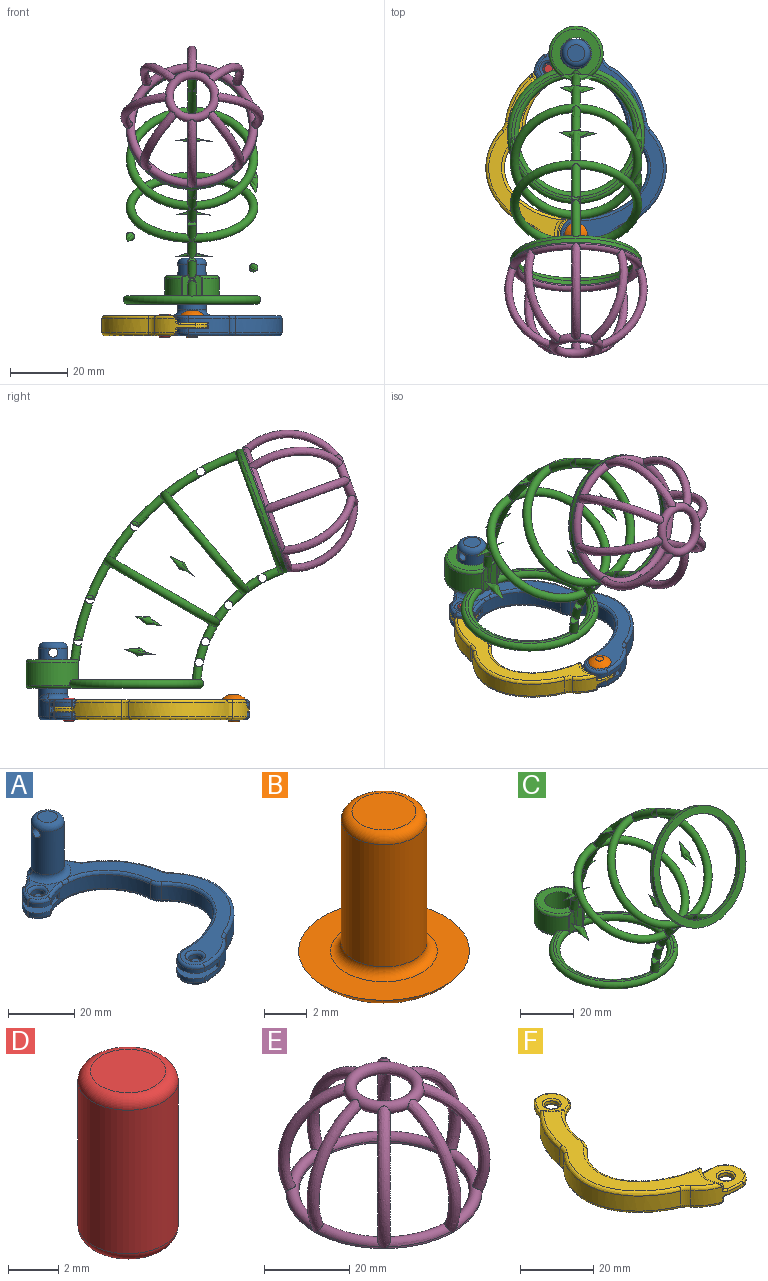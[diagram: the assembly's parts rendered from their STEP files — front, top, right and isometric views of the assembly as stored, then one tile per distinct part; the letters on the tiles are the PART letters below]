
ASSEMBLY  parts=6 mates=4
PART A: 90 faces, bbox 46.6x74.3x27 mm
  f0: plane 12.46x10.26mm, normal (0,0,1), area 30.7mm2, adj f19,f52,f55,f58,f59,f61,f85
  f1: plane 12.06x11.22mm, normal (0,0,-1), area 96.4mm2, adj f4,f12,f13,f14,f23,f88,f89
  f2: plane 12x11.67mm, normal (0,0,-1), area 80.9mm2, adj f8,f9,f10,f11,f15,f24,f38,f53
  f3: cylinder r=5mm len=18mm, axis (0,0,-1), area 498.6mm2, adj f18,f19,f20,f21,f22
  f4: extruded ~14.59x5.79mm, area 66.9mm2, adj f1,f14,f25,f27,f34,f46,f66,f89
  f5: extruded ~34.58x16.19mm, area 215.6mm2, adj f34,f35,f44,f71
  f6: extruded ~19.31x12.86mm, area 120.1mm2, adj f35,f36,f42,f76
  f7: extruded ~17.27x7.1mm, area 119.7mm2, adj f18,f20,f36,f38,f39,f40,f60,f80
  f8: cylinder r=5.28mm len=1.5mm, axis (0,0,-1), area 1.4mm2, adj f2,f9,f38,f59
  f9: extruded ~5.77x3.34mm, area 10.2mm2, adj f2,f8,f56,f58
  f10: cylinder r=5.28mm len=5.1mm, axis (0,0,-1), area 10.5mm2, adj f2,f53,f55,f56
  f11: extruded ~26.97x18.03mm, area 174.5mm2, adj f2,f26,f37,f50,f51,f52,f53,f67
  f12: extruded ~28.38x24.99mm, area 221.8mm2, adj f1,f14,f25,f27,f37,f48,f63,f88
  f13: cylinder r=2.1mm len=4.2mm, axis (0,0,-1), area 19.8mm2, adj f1,f84
  f14: cylinder r=5.53mm len=10.89mm, axis (0,0,-1), area 24mm2, adj f1,f4,f12,f47
  f15: cylinder r=2.1mm len=4.2mm, axis (0,0,-1), area 19.8mm2, adj f2,f85
  f16: plane 68.02x35.04mm, normal (0,0,1), area 436.8mm2, adj f19,f40,f41,f42,f43,f44,f45,f46
  f17: plane 6x6mm, normal (0,0,1), area 28.3mm2, adj f21
  f18: bspline ~6.9x3.63mm, area 7.6mm2, adj f3,f7,f19,f39
  f19: torus R=7mm, axis (0,0,1), area 67.5mm2, adj f0,f3,f16,f18,f20,f39,f51,f60
  f20: bspline ~6.9x3.63mm, area 7.6mm2, adj f3,f7,f19,f60
  f21: torus R=3mm, axis (0,0,1), area 84.4mm2, adj f3,f17
  f22: cylinder r=1.6mm len=10mm, axis (-1,0,0), area 100.5mm2, adj f3
  f23: cylinder r=6.53mm len=8.7mm, axis (0,0,1), area 19.2mm2, adj f1,f25,f88,f89
  f24: cylinder r=6.28mm len=7.95mm, axis (0,0,1), area 19.5mm2, adj f2,f26,f86,f87
  f25: plane 12.06x11.22mm, normal (0,0,1), area 96.4mm2, adj f4,f12,f23,f27,f32,f88,f89
  f26: plane 12x11.67mm, normal (0,0,1), area 80.9mm2, adj f11,f24,f28,f29,f30,f31,f38,f67
  f27: cylinder r=5.53mm len=10.89mm, axis (0,0,1), area 24mm2, adj f4,f12,f25,f64
  f28: cylinder r=5.28mm len=1.5mm, axis (0,0,1), area 1.4mm2, adj f26,f29,f38,f79
  f29: extruded ~5.77x3.34mm, area 10.2mm2, adj f26,f28,f72,f77
  f30: cylinder r=2.1mm len=4.2mm, axis (0,0,1), area 19.8mm2, adj f26,f83
  f31: cylinder r=5.28mm len=5.1mm, axis (0,0,1), area 10.5mm2, adj f26,f67,f72,f73
  f32: cylinder r=2.1mm len=4.2mm, axis (0,0,1), area 19.8mm2, adj f25,f82
  f33: plane 71.5x44.25mm, normal (0,0,-1), area 585.1mm2, adj f63,f64,f65,f66,f68,f69,f71,f73
  f34: cylinder r=5mm len=5mm, axis (0,0,-1), area 13.5mm2, adj f4,f5,f45,f69
  f35: cylinder r=5mm len=5mm, axis (0,0,-1), area 14.8mm2, adj f5,f6,f43,f74
  f36: cylinder r=5mm len=5mm, axis (0,0,-1), area 16.3mm2, adj f6,f7,f41,f78
  f37: cylinder r=5mm len=5mm, axis (0,0,-1), area 19mm2, adj f11,f12,f49,f65
  f38: cylinder r=5mm len=5mm, axis (0,0,-1), area 10.5mm2, adj f2,f7,f8,f26,f28,f61,f62,f81
  f39: bspline ~5.42x5.06mm, area 4.4mm2, adj f7,f18,f19,f40
  f40: bspline ~5.76x3.77mm, area 5.9mm2, adj f7,f16,f39,f41
  f41: torus R=6mm, axis (0,0,1), area 5.5mm2, adj f16,f36,f40,f42
  f42: bspline ~21.43x15.78mm, area 37.2mm2, adj f6,f16,f41,f43
  f43: torus R=6mm, axis (0,0,1), area 5mm2, adj f16,f35,f42,f44
  f44: bspline ~37.16x17.56mm, area 66.6mm2, adj f5,f16,f43,f45
  f45: torus R=6mm, axis (0,0,1), area 4.6mm2, adj f16,f34,f44,f46
  f46: bspline ~16.58x6.76mm, area 25mm2, adj f4,f16,f45,f47
  f47: torus R=4.53mm, axis (0,0,1), area 23.4mm2, adj f14,f16,f46,f48
  f48: bspline ~30.58x29.82mm, area 73.9mm2, adj f12,f16,f47,f49
  f49: torus R=4mm, axis (0,0,1), area 5.5mm2, adj f16,f37,f48,f50
  f50: bspline ~21.54x18.95mm, area 42.7mm2, adj f11,f16,f49,f51
  f51: bspline ~4.13x1.09mm, area 3.8mm2, adj f11,f19,f50,f52
  f52: bspline ~10.03x4.26mm, area 13.5mm2, adj f0,f11,f51,f54
  f53: cylinder r=1mm len=1.5mm, axis (0,0,-1), area 0.9mm2, adj f2,f10,f11,f54
  f54: sphere r=1mm, area 0.6mm2, adj f52,f53,f55
  f55: torus R=4.28mm, axis (0,0,1), area 10.3mm2, adj f0,f10,f54,f57
  f56: cylinder r=1mm len=1.5mm, axis (0,0,-1), area 0.6mm2, adj f2,f9,f10,f57
  f57: sphere r=1mm, area 0.4mm2, adj f55,f56,f58
  f58: bspline ~8.05x4.71mm, area 10.1mm2, adj f0,f9,f57,f59
  f59: torus R=4.28mm, axis (0,0,1), area 1.2mm2, adj f0,f8,f58,f61
  f60: bspline ~4.67x4.16mm, area 4mm2, adj f7,f19,f20,f62
  f61: torus R=6mm, axis (0,0,1), area 5.4mm2, adj f0,f38,f59,f62
  f62: bspline ~1.64x1.52mm, area 0.3mm2, adj f19,f38,f60,f61
  f63: bspline ~31.81x29.82mm, area 73.9mm2, adj f12,f33,f64,f65
  f64: torus R=4.53mm, axis (0,0,1), area 23.4mm2, adj f27,f33,f63,f66
  f65: torus R=4mm, axis (0,0,1), area 5.5mm2, adj f33,f37,f63,f68
  f66: bspline ~16.58x6.76mm, area 25mm2, adj f4,f33,f64,f69
  f67: cylinder r=1mm len=1.5mm, axis (0,0,-1), area 0.9mm2, adj f11,f26,f31,f70
  f68: bspline ~29.86x21.54mm, area 60.1mm2, adj f11,f33,f65,f70
  f69: torus R=6mm, axis (0,0,1), area 4.6mm2, adj f33,f34,f66,f71
  f70: sphere r=1mm, area 0.6mm2, adj f67,f68,f73
  f71: bspline ~36.6x20.51mm, area 66.6mm2, adj f5,f33,f69,f74
  f72: cylinder r=1mm len=1.5mm, axis (0,0,1), area 0.6mm2, adj f26,f29,f31,f75
  f73: torus R=4.28mm, axis (0,0,1), area 10.3mm2, adj f31,f33,f70,f75
  f74: torus R=6mm, axis (0,0,1), area 5mm2, adj f33,f35,f71,f76
  f75: sphere r=1mm, area 0.4mm2, adj f72,f73,f77
  f76: bspline ~22.82x14.21mm, area 37.2mm2, adj f6,f33,f74,f78
  f77: bspline ~8.05x4.71mm, area 10.1mm2, adj f29,f33,f75,f79
  f78: torus R=6mm, axis (0,0,1), area 5.5mm2, adj f33,f36,f76,f80
  f79: torus R=4.28mm, axis (0,0,1), area 1.2mm2, adj f28,f33,f77,f81
  f80: bspline ~18.72x8.82mm, area 32.4mm2, adj f7,f33,f78,f81
  f81: torus R=6mm, axis (0,0,1), area 5.7mm2, adj f33,f38,f79,f80
  f82: torus R=3.1mm, axis (0,0,1), area 24.3mm2, adj f32,f33
  f83: torus R=3.1mm, axis (0,0,1), area 24.3mm2, adj f30,f33
  f84: torus R=3.1mm, axis (0,0,1), area 24.3mm2, adj f13,f16
  f85: torus R=3.1mm, axis (0,0,1), area 24.3mm2, adj f0,f15
  f86: cylinder r=0.5mm len=2mm, axis (0,0,-1), area 2mm2, adj f2,f24,f26,f38
  f87: cylinder r=0.5mm len=2mm, axis (0,0,-1), area 2.1mm2, adj f2,f11,f24,f26
  f88: cylinder r=0.5mm len=2mm, axis (0,0,-1), area 2.3mm2, adj f1,f12,f23,f25
  f89: cylinder r=0.5mm len=2mm, axis (0,0,-1), area 2.5mm2, adj f1,f4,f23,f25
PART B: 7 faces, bbox 8x8x9.5 mm
  f0: cylinder r=2mm len=7mm, axis (0,0,-1), area 88mm2, adj f4,f5
  f1: plane 3x3mm, normal (0,0,1), area 7.1mm2, adj f5
  f2: plane 2.81x2.81mm, normal (0,0,-1), area 6.2mm2, adj f6
  f3: plane 8.01x8.01mm, normal (0,0,1), area 30.6mm2, adj f4,f6
  f4: torus R=2.5mm, axis (0,0,1), area 10.8mm2, adj f0,f3
  f5: torus R=1.5mm, axis (0,0,1), area 9mm2, adj f0,f1
  f6: bspline ~8x8mm, area 53.8mm2, adj f2,f3
PART C: 37 faces, bbox 52x92.3x90.3 mm
  f0: cylinder r=9.5mm len=3.98mm, axis (0,0,-1), area 4.1mm2, adj f4,f5,f6,f21,f24
  f1: cylinder r=9.5mm len=3.98mm, axis (0,0,-1), area 4.1mm2, adj f4,f5,f6,f24,f26
  f2: plane 44.02x21.28mm, normal (0,0,1), area 61.6mm2, adj f5,f6,f34,f35
  f3: plane 44.02x21.28mm, normal (0,0,1), area 61.6mm2, adj f5,f6,f34,f35
  f4: plane 45x44.55mm, normal (0,0,-1), area 130.3mm2, adj f0,f1,f5,f6,f7,f36
  f5: torus R=22.5mm, axis (0,0,1), area 623.7mm2, adj f0,f1,f2,f3,f4,f34,f35,f36
  f6: torus R=21.5mm, axis (0,0,1), area 558.8mm2, adj f0,f1,f2,f3,f4,f7,f34,f35
  f7: torus R=43.5mm, axis (1,0,0), area 2.4mm2, adj f4,f6
  f8: torus R=21.5mm, axis (0,-0.17,0.98), area 1273.1mm2, adj f15,f34
  f9: torus R=21.5mm, axis (0,-0.34,0.94), area 1275.4mm2, adj f15,f34
  f10: torus R=21.5mm, axis (0,-0.5,0.87), area 1237.3mm2, adj f15,f34
  f11: torus R=21.5mm, axis (0,-0.64,0.77), area 1273.1mm2, adj f15,f34
  f12: torus R=21.5mm, axis (0,-0.77,0.64), area 1237.6mm2, adj f15,f34
  f13: torus R=21.5mm, axis (0,-0.87,0.5), area 1237.6mm2, adj f15,f34
  f14: plane 1.78x0.28mm, normal (0,-0.95,0.32), area 0.3mm2, adj f17,f34
  f15: torus R=86.5mm, axis (1,0,0), area 814.4mm2, adj f8,f9,f10,f11,f12,f13,f16,f17
  f16: plane 1.48x0.2mm, normal (0,-0.95,0.32), area 0.2mm2, adj f15,f20
  f17: torus R=21.5mm, axis (0,-0.94,0.34), area 619.6mm2, adj f14,f15,f19,f20,f34
  f18: plane 46x43.23mm, normal (0,-0.94,0.34), area 405.3mm2, adj f19,f20
  f19: cylinder r=23mm len=46mm, axis (0,0.94,-0.34), area 216.8mm2, adj f17,f18
  f20: cylinder r=20mm len=40mm, axis (0,0.94,-0.34), area 187.7mm2, adj f15,f16,f17,f18
  f21: cylinder r=1mm len=8.52mm, axis (0,0,1), area 4.8mm2, adj f0,f22,f23,f33,f35
  f22: sphere r=1mm, area 0.6mm2, adj f21,f24,f32
  f23: torus R=8.5mm, axis (0,0,1), area 81.4mm2, adj f15,f21,f26,f29,f31,f33,f35
  f24: torus R=8.5mm, axis (0,0,1), area 78.3mm2, adj f0,f1,f22,f27,f28,f35
  f25: torus R=21mm, axis (0,0,1), area 4mm2, adj f15,f27,f28,f31
  f26: cylinder r=1mm len=8.52mm, axis (0,0,1), area 4.8mm2, adj f1,f23,f27,f31,f35
  f27: sphere r=1mm, area 0.6mm2, adj f24,f25,f26
  f28: plane 17x17mm, normal (0,0,-1), area 129.4mm2, adj f15,f24,f25,f30,f32
  f29: plane 17x16.91mm, normal (0,0,1), area 125.9mm2, adj f15,f23,f30
  f30: cylinder r=5.5mm len=11mm, axis (0,0,-1), area 345.6mm2, adj f28,f29
  f31: cylinder r=20mm len=8.99mm, axis (0,0,-1), area 23.4mm2, adj f15,f23,f25,f26
  f32: torus R=21mm, axis (0,0,1), area 4mm2, adj f15,f22,f28,f33
  f33: cylinder r=20mm len=8.99mm, axis (0,0,-1), area 23.4mm2, adj f15,f21,f23,f32
  f34: torus R=43.5mm, axis (1,0,0), area 371.9mm2, adj f2,f3,f5,f6,f8,f9,f10,f11
  f35: cylinder r=9.5mm len=19mm, axis (0,0,-1), area 397.2mm2, adj f2,f3,f5,f6,f21,f23,f24,f26
  f36: torus R=43.5mm, axis (1,0,0), area 0.1mm2, adj f4,f5
PART D: 5 faces, bbox 4.3x4.3x8 mm
  f0: cylinder r=2mm len=7mm, axis (0,0,-1), area 88mm2, adj f3,f4
  f1: plane 3x3mm, normal (0,0,1), area 7.1mm2, adj f4
  f2: plane 3x3mm, normal (0,0,-1), area 7.1mm2, adj f3
  f3: torus R=1.5mm, axis (0,0,1), area 9mm2, adj f0,f2
  f4: torus R=1.5mm, axis (0,0,1), area 9mm2, adj f0,f1
PART E: 20 faces, bbox 49.8x49.8x32 mm
  f0: cylinder r=23mm len=16.26mm, axis (0,0,-1), area 8.6mm2, adj f7,f11,f18,f19
  f1: cylinder r=23mm len=16.26mm, axis (0,0,-1), area 8.6mm2, adj f11,f17,f18,f19
  f2: cylinder r=23mm len=16.26mm, axis (0,0,-1), area 8.6mm2, adj f11,f16,f17,f19
  f3: cylinder r=23mm len=16.26mm, axis (0,0,-1), area 8.6mm2, adj f11,f15,f16,f19
  f4: cylinder r=23mm len=16.26mm, axis (0,0,-1), area 8.6mm2, adj f11,f14,f15,f19
  f5: cylinder r=23mm len=16.26mm, axis (0,0,-1), area 8.6mm2, adj f11,f13,f14,f19
  f6: cylinder r=23mm len=16.26mm, axis (0,0,-1), area 8.6mm2, adj f11,f12,f13,f19
  f7: bspline ~31.47x13.45mm, area 313.3mm2, adj f0,f8,f9,f11
  f8: torus R=8mm, axis (0,0,-1), area 414.1mm2, adj f7,f12,f13,f14,f15,f16,f17,f18
  f9: cylinder r=23mm len=16.26mm, axis (0,0,-1), area 8.6mm2, adj f7,f11,f12,f19
  f10: cylinder r=20mm len=40mm, axis (0,0,-1), area 62.8mm2, adj f11,f19
  f11: torus R=21.5mm, axis (0,0,1), area 579.4mm2, adj f0,f1,f2,f3,f4,f5,f6,f7
  f12: bspline ~31.47x17.03mm, area 313.5mm2, adj f6,f8,f9,f11
  f13: bspline ~31.47x13.45mm, area 313.3mm2, adj f5,f6,f8,f11
  f14: bspline ~31.47x17.03mm, area 313.3mm2, adj f4,f5,f8,f11
  f15: bspline ~31.47x13.45mm, area 313.3mm2, adj f3,f4,f8,f11
  f16: bspline ~31.47x17.03mm, area 313.3mm2, adj f2,f3,f8,f11
  f17: bspline ~31.47x13.45mm, area 313.3mm2, adj f1,f2,f8,f11
  f18: bspline ~31.47x17.03mm, area 313.3mm2, adj f0,f1,f8,f11
  f19: plane 46x46mm, normal (0,0,-1), area 405.3mm2, adj f0,f1,f2,f3,f4,f5,f6,f9
PART F: 95 faces, bbox 37.5x69.2x7.1 mm
  f0: extruded ~17.37x9.95mm, area 96.2mm2, adj f16,f20,f27,f36,f55,f58,f60,f76
  f1: extruded ~34.58x16.19mm, area 215.6mm2, adj f20,f21,f31,f40
  f2: extruded ~14.59x5.79mm, area 54mm2, adj f17,f21,f30,f41,f49,f50,f51,f86
  f3: cylinder r=6.53mm len=8.7mm, axis (0,0,1), area 9.6mm2, adj f28,f83,f87,f89
  f4: extruded ~28.38x24.99mm, area 214.1mm2, adj f17,f22,f26,f37,f44,f45,f46,f82
  f5: extruded ~17.03x12.28mm, area 85.3mm2, adj f22,f23,f33,f57,f59,f61,f66,f72
  f6: cylinder r=6.28mm len=3.9mm, axis (0,0,1), area 5.5mm2, adj f25,f55,f56,f57
  f7: plane 57.37x24.86mm, normal (0,0,-1), area 312.5mm2, adj f23,f24,f25,f26,f27,f28,f29,f30
  f8: plane 11.06x10.08mm, normal (0,0,-1), area 70.3mm2, adj f82,f84,f86,f87,f94
  f9: plane 10.45x10.24mm, normal (0,0,-1), area 52.1mm2, adj f56,f60,f61,f62,f63,f93
  f10: cylinder r=6.53mm len=8.7mm, axis (0,0,-1), area 9.6mm2, adj f39,f44,f48,f51
  f11: cylinder r=6.28mm len=3.9mm, axis (0,0,-1), area 5.5mm2, adj f34,f73,f77,f79
  f12: plane 57.37x24.86mm, normal (0,0,1), area 312.5mm2, adj f33,f34,f35,f36,f37,f38,f39,f40
  f13: plane 10.45x10.24mm, normal (0,0,1), area 52.1mm2, adj f68,f72,f74,f76,f77,f91
  f14: plane 11.06x10.08mm, normal (0,0,1), area 70.3mm2, adj f45,f47,f48,f49,f92
  f15: cylinder r=5.28mm len=8.52mm, axis (0,0,1), area 13.5mm2, adj f63,f66,f67,f68
  f16: extruded ~5.9x3.3mm, area 6.9mm2, adj f0,f62,f67,f74
  f17: cylinder r=5.53mm len=10.89mm, axis (0,0,1), area 16mm2, adj f2,f4,f47,f84
  f18: cylinder r=2.1mm len=4.2mm, axis (0,0,1), area 13.2mm2, adj f91,f93
  f19: cylinder r=2.1mm len=4.2mm, axis (0,0,1), area 13.2mm2, adj f92,f94
  f20: cylinder r=5mm len=5mm, axis (0,0,1), area 14.8mm2, adj f0,f1,f29,f38
  f21: cylinder r=5mm len=5mm, axis (0,0,1), area 13.5mm2, adj f1,f2,f32,f42
  f22: cylinder r=5mm len=5mm, axis (0,0,1), area 19mm2, adj f4,f5,f24,f35
  f23: bspline ~17.84x8.82mm, area 24.1mm2, adj f5,f7,f24,f54
  f24: torus R=4mm, axis (0,0,1), area 5.5mm2, adj f7,f22,f23,f26
  f25: torus R=7.28mm, axis (0,0,1), area 8mm2, adj f6,f7,f53,f54
  f26: bspline ~31.72x23.49mm, area 65.9mm2, adj f4,f7,f24,f81
  f27: bspline ~21.13x11.59mm, area 28.4mm2, adj f0,f7,f29,f53
  f28: torus R=7.53mm, axis (0,0,1), area 14.1mm2, adj f3,f7,f81,f90
  f29: torus R=6mm, axis (0,0,1), area 5mm2, adj f7,f20,f27,f31
  f30: bspline ~9.33x7.28mm, area 12.6mm2, adj f2,f7,f32,f90
  f31: bspline ~36.6x20.51mm, area 66.6mm2, adj f1,f7,f29,f32
  f32: torus R=6mm, axis (0,0,1), area 4.6mm2, adj f7,f21,f30,f31
  f33: bspline ~17.84x8.82mm, area 24.1mm2, adj f5,f12,f35,f70
  f34: torus R=7.28mm, axis (0,0,1), area 8mm2, adj f11,f12,f70,f80
  f35: torus R=4mm, axis (0,0,1), area 5.5mm2, adj f12,f22,f33,f37
  f36: bspline ~21.13x11.59mm, area 28.4mm2, adj f0,f12,f38,f80
  f37: bspline ~30.5x23.49mm, area 65.9mm2, adj f4,f12,f35,f43
  f38: torus R=6mm, axis (0,0,1), area 5mm2, adj f12,f20,f36,f40
  f39: torus R=7.53mm, axis (0,0,1), area 14.1mm2, adj f10,f12,f43,f52
  f40: bspline ~37.16x17.56mm, area 66.6mm2, adj f1,f12,f38,f42
  f41: bspline ~9.33x7.28mm, area 12.6mm2, adj f2,f12,f42,f52
  f42: torus R=6mm, axis (0,0,1), area 4.6mm2, adj f12,f21,f40,f41
  f43: bspline ~2.24x1.13mm, area 1mm2, adj f37,f39,f44
  f44: cylinder r=0.5mm len=1mm, axis (0,0,1), area 1.2mm2, adj f4,f10,f43,f46
  f45: bspline ~10.94x1.15mm, area 2.4mm2, adj f4,f14,f46,f47
  f46: bspline ~1.87x1.18mm, area 1.4mm2, adj f4,f44,f45,f48
  f47: torus R=5.03mm, axis (0,0,1), area 12.1mm2, adj f14,f17,f45,f49
  f48: torus R=6.03mm, axis (0,0,1), area 8.3mm2, adj f10,f14,f46,f50
  f49: bspline ~8.3x1.18mm, area 4.3mm2, adj f2,f14,f47,f50
  f50: bspline ~2.83x1.42mm, area 1.7mm2, adj f2,f48,f49,f51
  f51: cylinder r=0.5mm len=1mm, axis (0,0,1), area 1.2mm2, adj f2,f10,f50,f52
  f52: bspline ~2.36x1.84mm, area 1.2mm2, adj f39,f41,f51
  f53: bspline ~1.68x1.08mm, area 0.8mm2, adj f25,f27,f55
  f54: bspline ~1.91x1.09mm, area 0.9mm2, adj f23,f25,f57
  f55: cylinder r=0.5mm len=1mm, axis (0,0,1), area 1mm2, adj f0,f6,f53,f58
  f56: torus R=5.78mm, axis (0,0,1), area 4.6mm2, adj f6,f9,f58,f59
  f57: cylinder r=0.5mm len=1mm, axis (0,0,1), area 1.1mm2, adj f5,f6,f54,f59
  f58: bspline ~1.23x1.06mm, area 1mm2, adj f0,f55,f56,f60
  f59: bspline ~1.2x1.19mm, area 1.1mm2, adj f5,f56,f57,f61
  f60: bspline ~4.72x3.98mm, area 0.7mm2, adj f0,f9,f58,f62
  f61: bspline ~6.28x3.89mm, area 4.3mm2, adj f5,f9,f59,f64
  f62: bspline ~8.39x4.46mm, area 5.4mm2, adj f9,f16,f60,f65
  f63: torus R=4.78mm, axis (0,0,1), area 10.2mm2, adj f9,f15,f64,f65
  f64: sphere r=0.5mm, area 0.1mm2, adj f61,f63,f66
  f65: sphere r=0.5mm, area 0.1mm2, adj f62,f63,f67
  f66: cylinder r=0.5mm len=1mm, axis (0,0,1), area 0.3mm2, adj f5,f15,f64,f69
  f67: cylinder r=0.5mm len=1mm, axis (0,0,1), area 0.2mm2, adj f15,f16,f65,f71
  f68: torus R=4.78mm, axis (0,0,1), area 10.2mm2, adj f13,f15,f69,f71
  f69: sphere r=0.5mm, area 0.1mm2, adj f66,f68,f72
  f70: bspline ~1.91x1.09mm, area 0.9mm2, adj f33,f34,f73
  f71: sphere r=0.5mm, area 0.1mm2, adj f67,f68,f74
  f72: bspline ~6.28x3.89mm, area 4.3mm2, adj f5,f13,f69,f75
  f73: cylinder r=0.5mm len=1mm, axis (0,0,1), area 1.1mm2, adj f5,f11,f70,f75
  f74: bspline ~8.39x4.46mm, area 5.4mm2, adj f13,f16,f71,f76
  f75: bspline ~1.19x1.19mm, area 1.1mm2, adj f5,f72,f73,f77
  f76: bspline ~4.72x3.98mm, area 0.7mm2, adj f0,f13,f74,f78
  f77: torus R=5.78mm, axis (0,0,1), area 4.6mm2, adj f11,f13,f75,f78
  f78: bspline ~1.21x1.19mm, area 1mm2, adj f0,f76,f77,f79
  f79: cylinder r=0.5mm len=1mm, axis (0,0,1), area 1mm2, adj f0,f11,f78,f80
  f80: bspline ~1.68x1.08mm, area 0.8mm2, adj f34,f36,f79
  f81: bspline ~2.24x1.13mm, area 1mm2, adj f26,f28,f83
  f82: bspline ~10.94x1.15mm, area 2.4mm2, adj f4,f8,f84,f85
  f83: cylinder r=0.5mm len=1mm, axis (0,0,1), area 1.2mm2, adj f3,f4,f81,f85
  f84: torus R=5.03mm, axis (0,0,1), area 12.1mm2, adj f8,f17,f82,f86
  f85: bspline ~2.31x1.14mm, area 1.4mm2, adj f4,f82,f83,f87
  f86: bspline ~8.3x1.18mm, area 4.3mm2, adj f2,f8,f84,f88
  f87: torus R=6.03mm, axis (0,0,1), area 8.3mm2, adj f3,f8,f85,f88
  f88: bspline ~2.16x1.36mm, area 1.7mm2, adj f2,f86,f87,f89
  f89: cylinder r=0.5mm len=1mm, axis (0,0,1), area 1.2mm2, adj f2,f3,f88,f90
  f90: bspline ~2.36x1.84mm, area 1.2mm2, adj f28,f30,f89
  f91: torus R=2.6mm, axis (0,0,1), area 11.3mm2, adj f13,f18
  f92: torus R=2.6mm, axis (0,0,1), area 11.3mm2, adj f14,f19
  f93: torus R=2.6mm, axis (0,0,1), area 11.3mm2, adj f9,f18
  f94: torus R=2.6mm, axis (0,0,1), area 11.3mm2, adj f8,f19
PLACE A at identity
PLACE B rot(axis=(1,0,0),180deg) t=(-0.14,-23.03,2.7)mm
PLACE C t=(0,11.56,6.45)mm
PLACE D t=(-9.58,34.62,-5)mm
PLACE E rot(axis=(1,0,0),70deg) t=(0,-33.97,68.73)mm
PLACE F at identity
MATE fastened D.f0 <-> F.f6  axis (0,0,-1) through (-9.58,34.62,-1)mm
MATE fastened B.f0 <-> A.f13  axis (0,0,-1) through (0,-23.03,2.7)mm
MATE revolute C.f30 <-> A.f3  axis (0,0,-1) through (0,40.06,6.45)mm
MATE fastened C.f19 <-> E.f8  axis (0,-0.94,0.34) through (0,-33.97,68.73)mm
